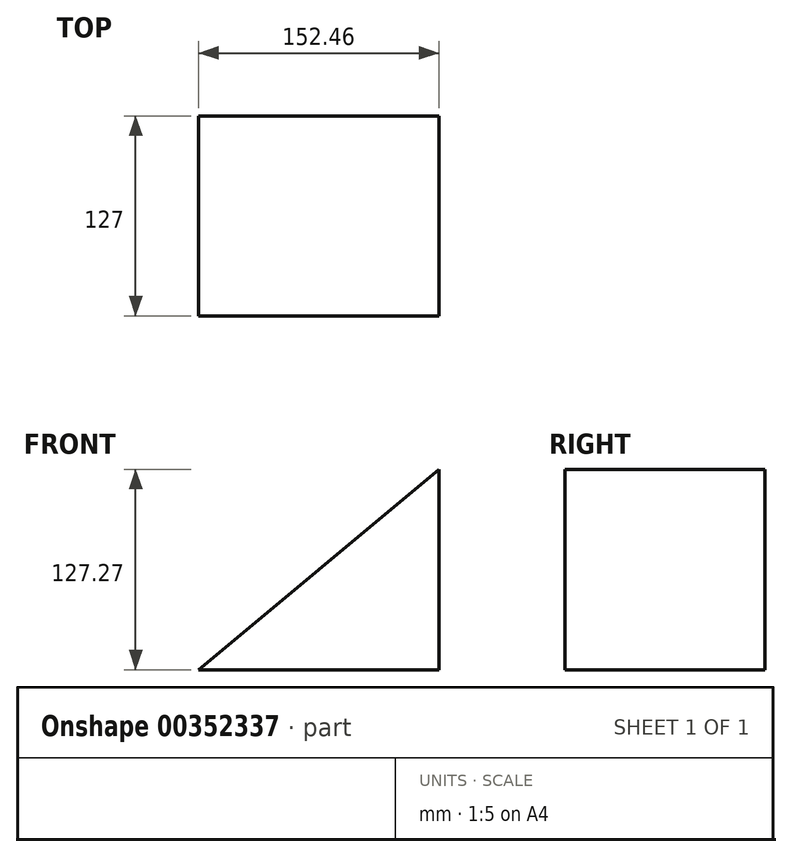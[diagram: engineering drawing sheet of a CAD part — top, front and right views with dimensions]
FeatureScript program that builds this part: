
annotation { "Feature Type Name" : "Feature", "Feature Type Description" : "" }
export const myFeature = defineFeature(function(context is Context, id is Id, definition is map)
    precondition{}
    {
        {
            var Q0;
            Q0=qCreatedBy(makeId("Front.planeOp"),FACE);
            var sketch = newSketch(context, id + "F0", { "sketchPlane" : qUnion([Q0])});
            skLineSegment(sketch, "E0", {"start": v(-76.14, 0) * mm, "end": v(76.32, 0) * mm});
            skLineSegment(sketch, "E1", {"start": v(76.32, 0) * mm, "end": v(76.32, 127.27) * mm});
            skLineSegment(sketch, "E2", {"start": v(76.32, 127.27) * mm, "end": v(-76.14, 0) * mm});
            skSolve(sketch);
        }
        {
            var Q0;
            Q0=makeQuery(id+"F0.imprint","IMPRINT",FACE,{"disambiguationData":[TD([[makeQuery(id+"F0.imprint","IMPRINT",EDGE,{"derivedFrom":sQuery(id+"F0.wireOp",EDGE,"E0")}),1.0]])]});
            extrude(context, id + "F1", {"entities" : qUnion([Q0]), "depth" : 127 * mm});
        }
    });
